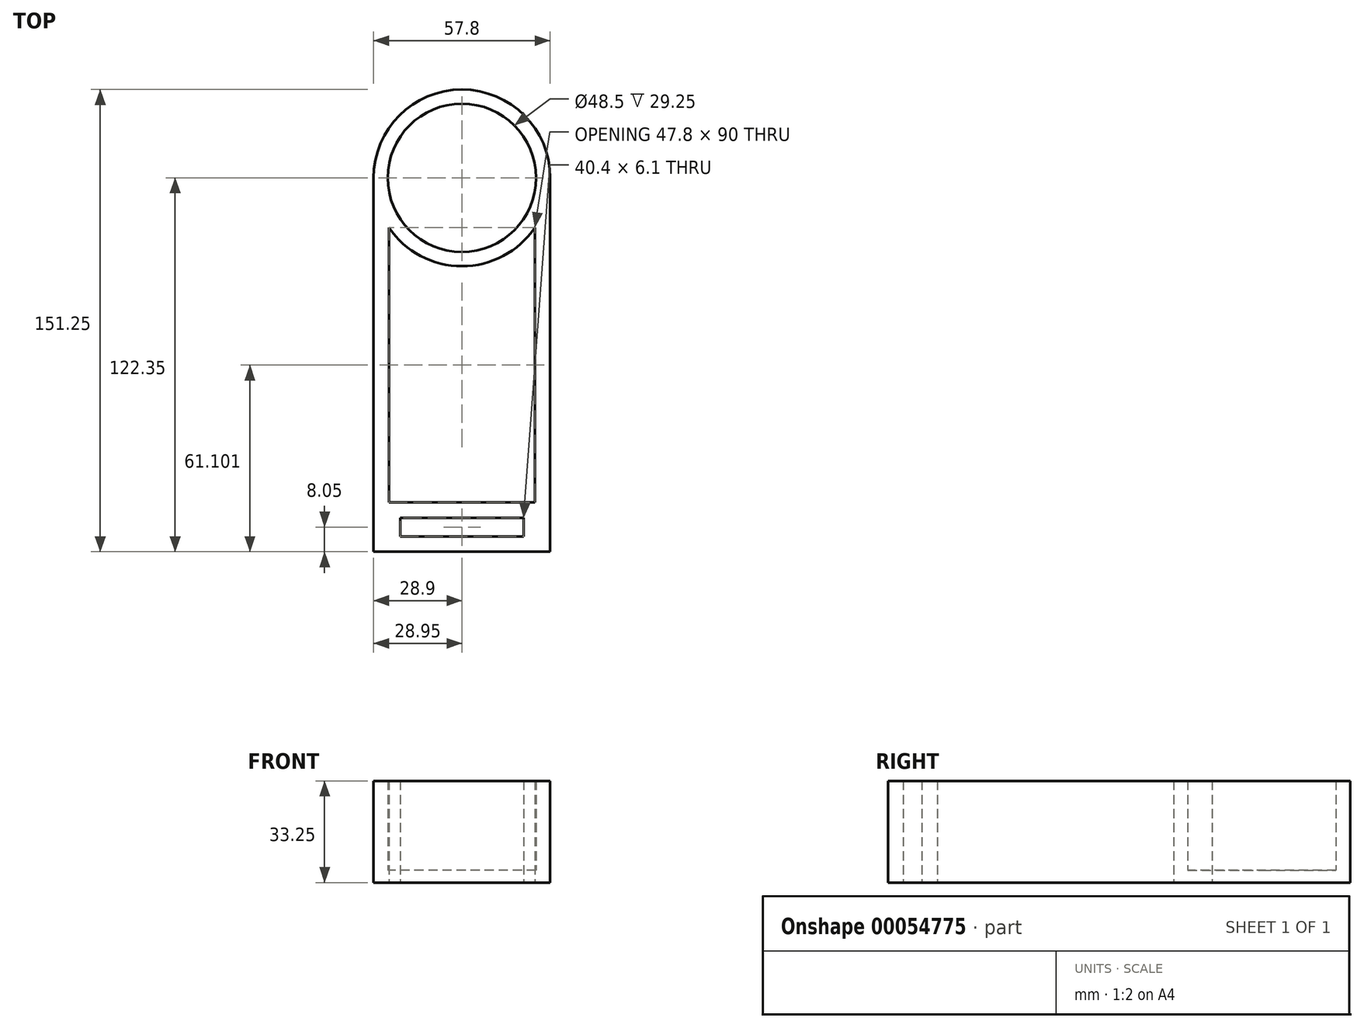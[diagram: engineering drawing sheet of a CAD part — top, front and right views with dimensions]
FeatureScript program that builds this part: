
annotation { "Feature Type Name" : "Feature", "Feature Type Description" : "" }
export const myFeature = defineFeature(function(context is Context, id is Id, definition is map)
    precondition{}
    {
        {
            var Q0;
            Q0=qCreatedBy(makeId("Top.planeOp"),FACE);
            var sketch = newSketch(context, id + "F0", { "sketchPlane" : qUnion([Q0])});
            skCircle(sketch, "E0", {"center": v(0, 0) * mm, "radius": 24.25 * mm});
            skCircle(sketch, "E1", {"center": v(0, 0) * mm, "radius": 28.9 * mm});
            skSolve(sketch);
        }
        {
            var Q0;
            Q0=makeQuery(id+"F0.imprint","IMPRINT",FACE,{"disambiguationData":[TD([[makeQuery(id+"F0.imprint","IMPRINT",EDGE,{"derivedFrom":sQuery(id+"F0.wireOp",EDGE,"E0")}),-1.0]])]});
            extrude(context, id + "F1", {"entities" : qUnion([Q0]), "depth" : 33.25 * mm});
        }
        {
            var Q0;
            Q0=qCreatedBy(makeId("Top.planeOp"),FACE);
            var sketch = newSketch(context, id + "F2", { "sketchPlane" : qUnion([Q0])});
            skCircle(sketch, "E2.0", {"center": v(0, 0) * mm, "radius": 28.9 * mm});
            skSolve(sketch);
        }
        {
            var Q0;
            Q0=makeQuery(id+"F2.imprint","IMPRINT",FACE,{"disambiguationData":[TD([[makeQuery(id+"F2.imprint","IMPRINT",EDGE,{"derivedFrom":sQuery(id+"F2.wireOp",EDGE,"E2.0")}),1.0]])]});
            extrude(context, id + "F3", {"entities" : qUnion([Q0]), "operationType" : NewBodyOperationType.ADD, "depth" : 4 * mm});
        }
        {
            var Q0;
            Q0=qCreatedBy(makeId("Top.planeOp"),FACE);
            var sketch = newSketch(context, id + "F4", { "sketchPlane" : qUnion([Q0])});
            skCircle(sketch, "E3.0", {"center": v(0, 0) * mm, "radius": 28.9 * mm});
            skLineSegment(sketch, "E4", {"start": v(-28.9, 0) * mm, "end": v(-28.9, -73) * mm});
            skLineSegment(sketch, "E5", {"start": v(28.9, 0) * mm, "end": v(28.9, -73) * mm});
            skLineSegment(sketch, "E6", {"start": v(-23.9, -16.25) * mm, "end": v(-23.9, -66.32) * mm});
            skLineSegment(sketch, "E7", {"start": v(23.9, -66.32) * mm, "end": v(23.9, -16.25) * mm});
            skLineSegment(sketch, "E8", {"start": v(-28.9, -73) * mm, "end": v(-28.9, -88.68) * mm});
            skLineSegment(sketch, "E9", {"start": v(28.9, -73) * mm, "end": v(28.9, -88.68) * mm});
            skLineSegment(sketch, "E10.bottom", {"start": v(-20.15, -111.25) * mm, "end": v(20.25, -111.25) * mm});
            skLineSegment(sketch, "E10.top", {"start": v(-20.15, -117.35) * mm, "end": v(20.25, -117.35) * mm});
            skLineSegment(sketch, "E10.left", {"start": v(-20.15, -111.25) * mm, "end": v(-20.15, -117.35) * mm});
            skLineSegment(sketch, "E10.right", {"start": v(20.25, -111.25) * mm, "end": v(20.25, -117.35) * mm});
            skLineSegment(sketch, "E11", {"start": v(-28.9, -88.68) * mm, "end": v(-28.9, -122.35) * mm});
            skLineSegment(sketch, "E12", {"start": v(-28.9, -122.35) * mm, "end": v(36.4, -122.35) * mm});
            skLineSegment(sketch, "E13", {"start": v(28.9, -88.68) * mm, "end": v(28.9, -122.35) * mm});
            skLineSegment(sketch, "E14", {"start": v(23.9, -66.32) * mm, "end": v(23.9, -106.25) * mm});
            skLineSegment(sketch, "E15", {"start": v(23.9, -106.25) * mm, "end": v(-23.9, -106.25) * mm});
            skLineSegment(sketch, "E16", {"start": v(-23.9, -66.32) * mm, "end": v(-23.9, -106.25) * mm});
            skSolve(sketch);
        }
        {
            var Q0;
            {var subQ4=sQuery(id+"F4.wireOp",EDGE,"E4");Q0=makeQuery(id+"F4.imprint","IMPRINT",FACE,{"disambiguationData":[TD([[makeQuery(id+"F4.imprint","IMPRINT",EDGE,{"derivedFrom":subQ4}),1.0]])]});}
            var Q1;
            Q1=makeQuery(id+"F1.opExtrude","CAP_FACE",FACE,{"disambiguationData":[OSD([sQuery(id+"F0.wireOp",EDGE,"E0"),sQuery(id+"F0.wireOp",EDGE,"E1")])],"isStart":false});
            extrude(context, id + "F5", {"entities" : qUnion([Q0]), "operationType" : NewBodyOperationType.ADD, "endBound" : BoundingType.UP_TO_SURFACE, "endBoundEntityFace" : qUnion([Q1]), "depth" : 33 * mm});
        }
    });
